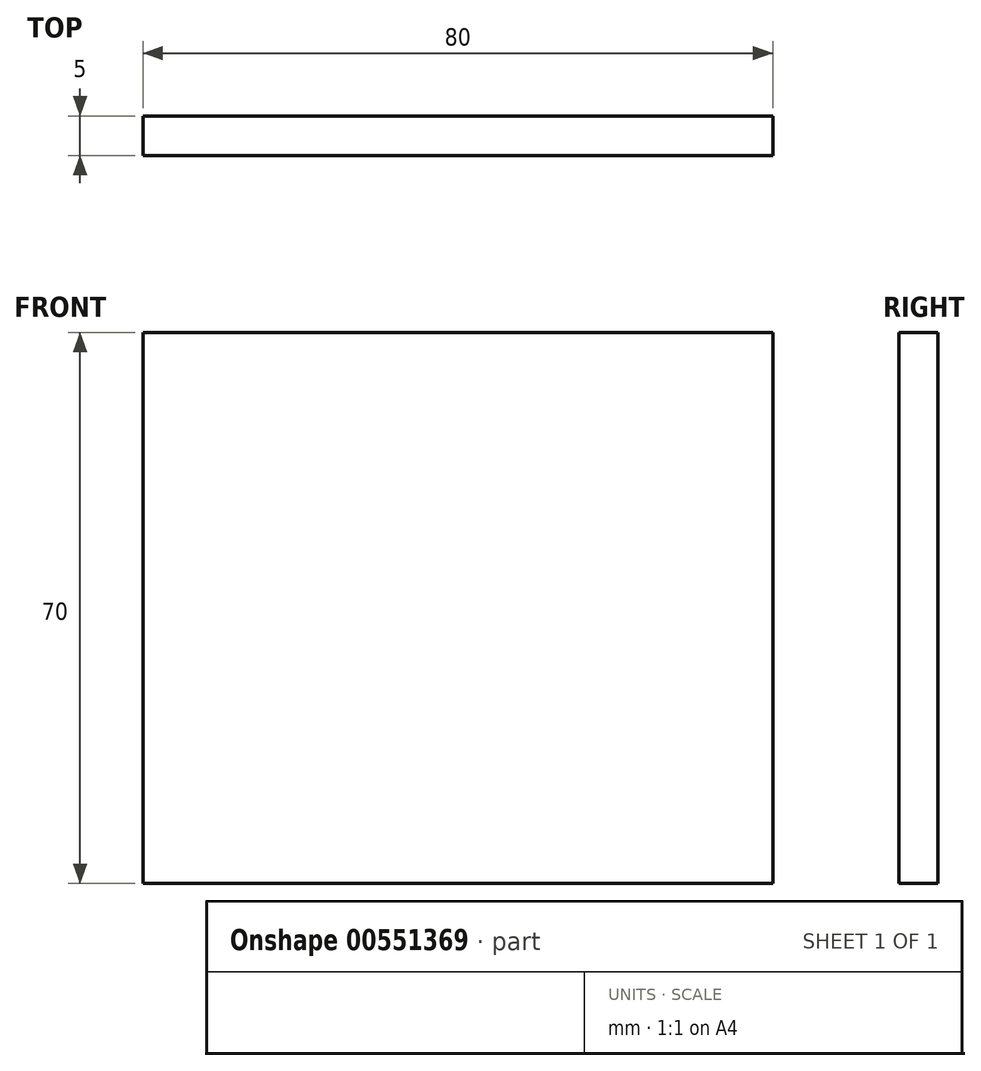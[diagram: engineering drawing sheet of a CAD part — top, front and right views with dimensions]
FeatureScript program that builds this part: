
annotation { "Feature Type Name" : "Feature", "Feature Type Description" : "" }
export const myFeature = defineFeature(function(context is Context, id is Id, definition is map)
    precondition{}
    {
        {
            var Q0;
            Q0=qCreatedBy(makeId("Front.planeOp"),FACE);
            var sketch = newSketch(context, id + "F0", { "sketchPlane" : qUnion([Q0])});
            skLineSegment(sketch, "E0.bottom", {"start": v(-41.38, 45.1) * mm, "end": v(38.62, 45.1) * mm});
            skLineSegment(sketch, "E0.top", {"start": v(-41.38, -24.9) * mm, "end": v(38.62, -24.9) * mm});
            skLineSegment(sketch, "E0.left", {"start": v(-41.38, 45.1) * mm, "end": v(-41.38, -24.9) * mm});
            skLineSegment(sketch, "E0.right", {"start": v(38.62, 45.1) * mm, "end": v(38.62, -24.9) * mm});
            skSolve(sketch);
        }
        {
            var Q0;
            Q0 = qSketchRegion(id + "F0", true);
            extrude(context, id + "F1", {"entities" : qUnion([Q0]), "depth" : 5 * mm, "offsetDistance" : 25 * mm});
        }
    });
